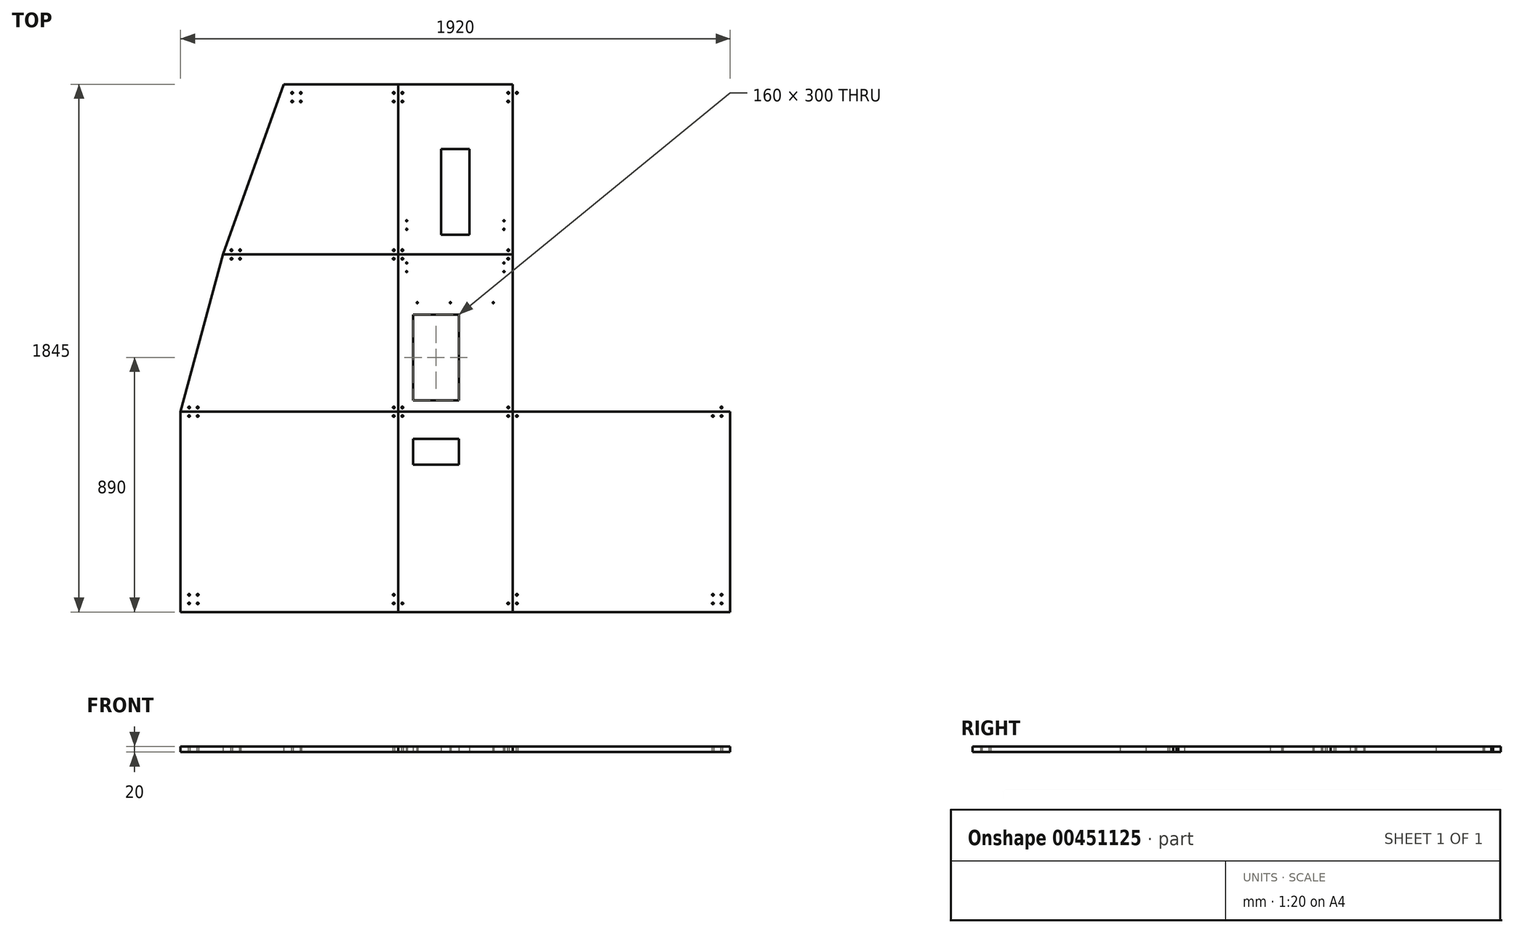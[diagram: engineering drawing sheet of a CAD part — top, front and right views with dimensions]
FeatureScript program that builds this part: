
annotation { "Feature Type Name" : "Feature", "Feature Type Description" : "" }
export const myFeature = defineFeature(function(context is Context, id is Id, definition is map)
    precondition{}
    {
        {
            var Q0;
            Q0=qCreatedBy(makeId("Top.planeOp"),FACE);
            var sketch = newSketch(context, id + "F0", { "sketchPlane" : qUnion([Q0])});
            skLineSegment(sketch, "E0.bottom", {"start": v(200, -350) * mm, "end": v(-200, -350) * mm});
            skLineSegment(sketch, "E0.top", {"start": v(200, 350) * mm, "end": v(-200, 350) * mm});
            skLineSegment(sketch, "E0.left", {"start": v(200, -350) * mm, "end": v(200, 350) * mm});
            skLineSegment(sketch, "E0.right", {"start": v(-200, -350) * mm, "end": v(-200, 350) * mm});
            skPoint(sketch, "E0.middle", {"position": v(0, 0) * mm});
            skCircle(sketch, "E1", {"center": v(185, 335) * mm, "radius": 3 * mm});
            skCircle(sketch, "E2", {"center": v(-185, 335) * mm, "radius": 3 * mm});
            skCircle(sketch, "E3", {"center": v(185, -320) * mm, "radius": 3 * mm});
            skCircle(sketch, "E4", {"center": v(-185, -320) * mm, "radius": 3 * mm});
            skLineSegment(sketch, "E5.bottom", {"start": v(12.5, 165.67) * mm, "end": v(-147.5, 165.67) * mm});
            skLineSegment(sketch, "E5.top", {"start": v(12.5, 255.63) * mm, "end": v(-147.5, 255.63) * mm});
            skLineSegment(sketch, "E5.left", {"start": v(12.5, 165.67) * mm, "end": v(12.5, 255.63) * mm});
            skLineSegment(sketch, "E5.right", {"start": v(-147.5, 165.67) * mm, "end": v(-147.5, 255.63) * mm});
            skPoint(sketch, "E5.middle", {"position": v(-67.5, 210.65) * mm});
            skSolve(sketch);
        }
        {
            var Q0;
            Q0=qSketchRegion(id+"F0",true);
            extrude(context, id + "F1", {"entities" : qUnion([Q0]), "depth" : 20 * mm});
        }
        {
            var Q0;
            Q0=qCreatedBy(makeId("Top.planeOp"),FACE);
            var sketch = newSketch(context, id + "F2", { "sketchPlane" : qUnion([Q0])});
            skLineSegment(sketch, "E6.top", {"start": v(-200, 900) * mm, "end": v(-812, 900) * mm});
            skLineSegment(sketch, "E6.left", {"start": v(-200, 350) * mm, "end": v(-200, 900) * mm});
            skPoint(sketch, "E6.middle", {"position": v(-506, 625) * mm});
            skLineSegment(sketch, "E7", {"start": v(-200, 350) * mm, "end": v(-960, 350) * mm});
            skLineSegment(sketch, "E8", {"start": v(-960, 350) * mm, "end": v(-812, 900) * mm});
            skCircle(sketch, "E9", {"center": v(-215, 885) * mm, "radius": 3 * mm});
            skCircle(sketch, "E10", {"center": v(-215, 365) * mm, "radius": 3 * mm});
            skCircle(sketch, "E11", {"center": v(-930, 365) * mm, "radius": 3 * mm});
            skCircle(sketch, "E12", {"center": v(-782, 885) * mm, "radius": 3 * mm});
            skLineSegment(sketch, "E13.left", {"start": v(-200, 900) * mm, "end": v(-200, 1495) * mm});
            skPoint(sketch, "E13.middle", {"position": v(-506, 1197.5) * mm});
            skLineSegment(sketch, "E14", {"start": v(-200, 1495) * mm, "end": v(-600, 1495) * mm});
            skLineSegment(sketch, "E15", {"start": v(-812, 900) * mm, "end": v(-600, 1495) * mm});
            skCircle(sketch, "E16", {"center": v(-215, 1465) * mm, "radius": 3 * mm});
            skCircle(sketch, "E17", {"center": v(-215, 915) * mm, "radius": 3 * mm});
            skCircle(sketch, "E18", {"center": v(-782, 915) * mm, "radius": 3 * mm});
            skCircle(sketch, "E19", {"center": v(-570, 1465) * mm, "radius": 3 * mm});
            skLineSegment(sketch, "E20", {"start": v(0, 1490.85) * mm, "end": v(0, 501.43) * mm, "construction": true});
            skCircle(sketch, "E21.MirrorC", {"center": v(215, 1465) * mm, "radius": 3 * mm});
            skCircle(sketch, "E22.MirrorC", {"center": v(930, 365) * mm, "radius": 3 * mm});
            skCircle(sketch, "E23.MirrorC", {"center": v(782, 885) * mm, "radius": 3 * mm});
            skCircle(sketch, "E24.MirrorC", {"center": v(782, 915) * mm, "radius": 3 * mm});
            skCircle(sketch, "E25.MirrorC", {"center": v(570, 1465) * mm, "radius": 3 * mm});
            skCircle(sketch, "E26.MirrorC", {"center": v(215, 885) * mm, "radius": 3 * mm});
            skCircle(sketch, "E27.MirrorC", {"center": v(215, 365) * mm, "radius": 3 * mm});
            skCircle(sketch, "E28.MirrorC", {"center": v(215, 915) * mm, "radius": 3 * mm});
            skLineSegment(sketch, "E29.MirrorCS", {"start": v(200, 1495) * mm, "end": v(600, 1495) * mm});
            skLineSegment(sketch, "E30.MirrorCS", {"start": v(960, 350) * mm, "end": v(812, 900) * mm});
            skLineSegment(sketch, "E31.MirrorCS", {"start": v(200, 900) * mm, "end": v(812, 900) * mm});
            skPoint(sketch, "E32.MirrorP", {"position": v(506, 1197.5) * mm});
            skLineSegment(sketch, "E33.MirrorCS", {"start": v(200, 350) * mm, "end": v(200, 900) * mm});
            skPoint(sketch, "E34.MirrorP", {"position": v(506, 625) * mm});
            skLineSegment(sketch, "E35.MirrorCS", {"start": v(200, 350) * mm, "end": v(960, 350) * mm});
            skLineSegment(sketch, "E36.MirrorCS", {"start": v(812, 900) * mm, "end": v(600, 1495) * mm});
            skLineSegment(sketch, "E37.MirrorCS", {"start": v(200, 900) * mm, "end": v(200, 1495) * mm});
            skCircle(sketch, "E38", {"center": v(-900, 365) * mm, "radius": 3 * mm});
            skCircle(sketch, "E39", {"center": v(-752, 885) * mm, "radius": 3 * mm});
            skCircle(sketch, "E40", {"center": v(-752, 915) * mm, "radius": 3 * mm});
            skCircle(sketch, "E41", {"center": v(-570, 1435) * mm, "radius": 3 * mm});
            skCircle(sketch, "E42", {"center": v(-540, 1465) * mm, "radius": 3 * mm});
            skCircle(sketch, "E43", {"center": v(-540, 1435) * mm, "radius": 3 * mm});
            skCircle(sketch, "E44", {"center": v(-215, 1435) * mm, "radius": 3 * mm});
            skCircle(sketch, "E45.MirrorC", {"center": v(215, 1435) * mm, "radius": 3 * mm});
            skCircle(sketch, "E46.MirrorC", {"center": v(540, 1465) * mm, "radius": 3 * mm});
            skCircle(sketch, "E47.MirrorC", {"center": v(540, 1435) * mm, "radius": 3 * mm});
            skCircle(sketch, "E48.MirrorC", {"center": v(570, 1435) * mm, "radius": 3 * mm});
            skCircle(sketch, "E49.MirrorC", {"center": v(752, 915) * mm, "radius": 3 * mm});
            skCircle(sketch, "E50.MirrorC", {"center": v(752, 885) * mm, "radius": 3 * mm});
            skCircle(sketch, "E51.MirrorC", {"center": v(900, 365) * mm, "radius": 3 * mm});
            skSolve(sketch);
        }
        {
            var Q0;
            Q0=makeQuery(id+"F2.imprint","IMPRINT",FACE,{"disambiguationData":[TD([[makeQuery(id+"F2.imprint","IMPRINT",EDGE,{"derivedFrom":sQuery(id+"F2.wireOp",EDGE,"E6.left")}),1.0]])]});
            var Q1;
            Q1=makeQuery(id+"F2.imprint","IMPRINT",FACE,{"disambiguationData":[TD([[makeQuery(id+"F2.imprint","IMPRINT",EDGE,{"derivedFrom":sQuery(id+"F2.wireOp",EDGE,"E22.MirrorC")}),1.0]])]});
            extrude(context, id + "F3", {"entities" : qUnion([Q0, Q1]), "depth" : 20 * mm});
        }
        {
            var Q0;
            Q0=makeQuery(id+"F2.imprint","IMPRINT",FACE,{"disambiguationData":[TD([[makeQuery(id+"F2.imprint","IMPRINT",EDGE,{"derivedFrom":sQuery(id+"F2.wireOp",EDGE,"E6.top")}),-1.0]])]});
            var Q1;
            Q1=makeQuery(id+"F2.imprint","IMPRINT",FACE,{"disambiguationData":[TD([[makeQuery(id+"F2.imprint","IMPRINT",EDGE,{"derivedFrom":sQuery(id+"F2.wireOp",EDGE,"E21.MirrorC")}),1.0]])]});
            extrude(context, id + "F4", {"entities" : qUnion([Q0, Q1]), "depth" : 20 * mm});
        }
        {
            var Q0;
            Q0=qCreatedBy(makeId("Top.planeOp"),FACE);
            var sketch = newSketch(context, id + "F5", { "sketchPlane" : qUnion([Q0])});
            skLineSegment(sketch, "E52.bottom", {"start": v(200, 900) * mm, "end": v(-200, 900) * mm});
            skLineSegment(sketch, "E52.top", {"start": v(200, 350) * mm, "end": v(-200, 350) * mm});
            skLineSegment(sketch, "E52.left", {"start": v(200, 900) * mm, "end": v(200, 350) * mm});
            skLineSegment(sketch, "E52.right", {"start": v(-200, 900) * mm, "end": v(-200, 350) * mm});
            skPoint(sketch, "E52.middle", {"position": v(0, 625) * mm});
            skCircle(sketch, "E53", {"center": v(-132.5, 731.5) * mm, "radius": 2.05 * mm});
            skCircle(sketch, "E54", {"center": v(-17.5, 731.5) * mm, "radius": 2.05 * mm});
            skCircle(sketch, "E55", {"center": v(132.5, 731.5) * mm, "radius": 2.05 * mm});
            skCircle(sketch, "E56", {"center": v(-185, 885) * mm, "radius": 3 * mm});
            skCircle(sketch, "E57", {"center": v(185, 885) * mm, "radius": 3 * mm});
            skCircle(sketch, "E58", {"center": v(-185, 365) * mm, "radius": 3 * mm});
            skCircle(sketch, "E59", {"center": v(185, 365) * mm, "radius": 3 * mm});
            skCircle(sketch, "E60", {"center": v(170, 870) * mm, "radius": 2.05 * mm});
            skCircle(sketch, "E61", {"center": v(170, 840) * mm, "radius": 2.05 * mm});
            skLineSegment(sketch, "E62", {"start": v(0, 625) * mm, "end": v(0, 499.57) * mm, "construction": true});
            skCircle(sketch, "E63.MirrorC", {"center": v(-170, 840) * mm, "radius": 2.05 * mm});
            skCircle(sketch, "E64.MirrorC", {"center": v(-170, 870) * mm, "radius": 2.05 * mm});
            skLineSegment(sketch, "E65.bottom", {"start": v(12.5, 390) * mm, "end": v(-147.5, 390) * mm});
            skLineSegment(sketch, "E65.top", {"start": v(12.5, 690) * mm, "end": v(-147.5, 690) * mm});
            skLineSegment(sketch, "E65.left", {"start": v(12.5, 390) * mm, "end": v(12.5, 690) * mm});
            skLineSegment(sketch, "E65.right", {"start": v(-147.5, 390) * mm, "end": v(-147.5, 690) * mm});
            skPoint(sketch, "E65.middle", {"position": v(-67.5, 540) * mm});
            skSolve(sketch);
        }
        {
            var Q0;
            Q0=qSketchRegion(id+"F5",true);
            extrude(context, id + "F6", {"entities" : qUnion([Q0]), "depth" : 20 * mm});
        }
        {
            var Q0;
            Q0=qCreatedBy(makeId("Top.planeOp"),FACE);
            var sketch = newSketch(context, id + "F7", { "sketchPlane" : qUnion([Q0])});
            skLineSegment(sketch, "E66.bottom", {"start": v(-200, 900) * mm, "end": v(200, 900) * mm});
            skLineSegment(sketch, "E66.top", {"start": v(200, 1495) * mm, "end": v(-200, 1495) * mm});
            skLineSegment(sketch, "E66.left", {"start": v(-200, 900) * mm, "end": v(-200, 1495) * mm});
            skLineSegment(sketch, "E66.right", {"start": v(200, 900) * mm, "end": v(200, 1495) * mm});
            skPoint(sketch, "E66.middle", {"position": v(0, 1197.5) * mm});
            skCircle(sketch, "E67", {"center": v(170, 970) * mm, "radius": 2.05 * mm, "construction": true});
            skCircle(sketch, "E68", {"center": v(170, 940) * mm, "radius": 2.05 * mm, "construction": true});
            skCircle(sketch, "E69", {"center": v(170, 988) * mm, "radius": 2.05 * mm});
            skCircle(sketch, "E70", {"center": v(170, 1018) * mm, "radius": 2.05 * mm});
            skCircle(sketch, "E71.MirrorC", {"center": v(-170, 970) * mm, "radius": 2.05 * mm, "construction": true});
            skCircle(sketch, "E72.MirrorC", {"center": v(-170, 988) * mm, "radius": 2.05 * mm});
            skCircle(sketch, "E73.MirrorC", {"center": v(-170, 1018) * mm, "radius": 2.05 * mm});
            skCircle(sketch, "E74.MirrorC", {"center": v(-170, 940) * mm, "radius": 2.05 * mm, "construction": true});
            skCircle(sketch, "E75", {"center": v(185, 1465) * mm, "radius": 3 * mm});
            skCircle(sketch, "E76", {"center": v(-185, 1465) * mm, "radius": 3 * mm});
            skCircle(sketch, "E77", {"center": v(185, 915) * mm, "radius": 3 * mm});
            skCircle(sketch, "E78", {"center": v(-185, 915) * mm, "radius": 3 * mm});
            skCircle(sketch, "E79", {"center": v(-185, 1435) * mm, "radius": 3 * mm});
            skCircle(sketch, "E80", {"center": v(185, 1435) * mm, "radius": 3 * mm});
            skLineSegment(sketch, "E81.bottom", {"start": v(50, 969.07) * mm, "end": v(-50, 969.07) * mm});
            skLineSegment(sketch, "E81.top", {"start": v(50, 1269.07) * mm, "end": v(-50, 1269.07) * mm});
            skLineSegment(sketch, "E81.left", {"start": v(50, 969.07) * mm, "end": v(50, 1269.07) * mm});
            skLineSegment(sketch, "E81.right", {"start": v(-50, 969.07) * mm, "end": v(-50, 1269.07) * mm});
            skPoint(sketch, "E81.middle", {"position": v(0, 1119.07) * mm});
            skSolve(sketch);
        }
        {
            var Q0;
            Q0=qSketchRegion(id+"F7",true);
            extrude(context, id + "F8", {"entities" : qUnion([Q0]), "depth" : 20 * mm});
        }
        {
            var Q0;
            Q0=qCreatedBy(makeId("Top.planeOp"),FACE);
            var sketch = newSketch(context, id + "F9", { "sketchPlane" : qUnion([Q0])});
            skLineSegment(sketch, "E82.bottom", {"start": v(-200, -350) * mm, "end": v(-960, -350) * mm});
            skLineSegment(sketch, "E82.top", {"start": v(-200, 350) * mm, "end": v(-960, 350) * mm});
            skLineSegment(sketch, "E82.left", {"start": v(-200, -350) * mm, "end": v(-200, 350) * mm});
            skLineSegment(sketch, "E82.right", {"start": v(-960, -350) * mm, "end": v(-960, 350) * mm});
            skPoint(sketch, "E82.middle", {"position": v(-580, 0) * mm});
            skPoint(sketch, "E83", {"position": v(-930, 335) * mm});
            skPoint(sketch, "E84", {"position": v(-215, 335) * mm});
            skPoint(sketch, "E85", {"position": v(-930, -320) * mm});
            skPoint(sketch, "E86", {"position": v(-215, -320) * mm});
            skCircle(sketch, "E87", {"center": v(-930, 335) * mm, "radius": 3 * mm});
            skCircle(sketch, "E88", {"center": v(-215, 335) * mm, "radius": 3 * mm});
            skCircle(sketch, "E89", {"center": v(-930, -320) * mm, "radius": 3 * mm});
            skCircle(sketch, "E90", {"center": v(-215, -320) * mm, "radius": 3 * mm});
            skLineSegment(sketch, "E91.bottom", {"start": v(200, -350) * mm, "end": v(960, -350) * mm});
            skLineSegment(sketch, "E91.top", {"start": v(200, 350) * mm, "end": v(960, 350) * mm});
            skLineSegment(sketch, "E91.left", {"start": v(200, -350) * mm, "end": v(200, 350) * mm});
            skLineSegment(sketch, "E91.right", {"start": v(960, -350) * mm, "end": v(960, 350) * mm});
            skPoint(sketch, "E91.middle", {"position": v(580, 0) * mm});
            skCircle(sketch, "E92", {"center": v(215, 335) * mm, "radius": 3 * mm});
            skCircle(sketch, "E93", {"center": v(930, 335) * mm, "radius": 3 * mm});
            skCircle(sketch, "E94", {"center": v(215, -320) * mm, "radius": 3 * mm});
            skCircle(sketch, "E95", {"center": v(930, -320) * mm, "radius": 3 * mm});
            skCircle(sketch, "E96", {"center": v(-930, -290) * mm, "radius": 3 * mm});
            skCircle(sketch, "E97", {"center": v(-900, -320) * mm, "radius": 3 * mm});
            skCircle(sketch, "E98", {"center": v(-900, -290) * mm, "radius": 3 * mm});
            skCircle(sketch, "E99", {"center": v(-215, -290) * mm, "radius": 3 * mm});
            skCircle(sketch, "E100", {"center": v(-900, 335) * mm, "radius": 3 * mm});
            skCircle(sketch, "E101", {"center": v(900, -320) * mm, "radius": 3 * mm});
            skCircle(sketch, "E102", {"center": v(930, -290) * mm, "radius": 3 * mm});
            skCircle(sketch, "E103", {"center": v(900, -290) * mm, "radius": 3 * mm});
            skCircle(sketch, "E104", {"center": v(215, -290) * mm, "radius": 3 * mm});
            skCircle(sketch, "E105", {"center": v(900, 335) * mm, "radius": 3 * mm});
            skSolve(sketch);
        }
        {
            var Q0;
            Q0=qSketchRegion(id+"F9",true);
            extrude(context, id + "F10", {"entities" : qUnion([Q0]), "depth" : 20 * mm});
        }
    });
